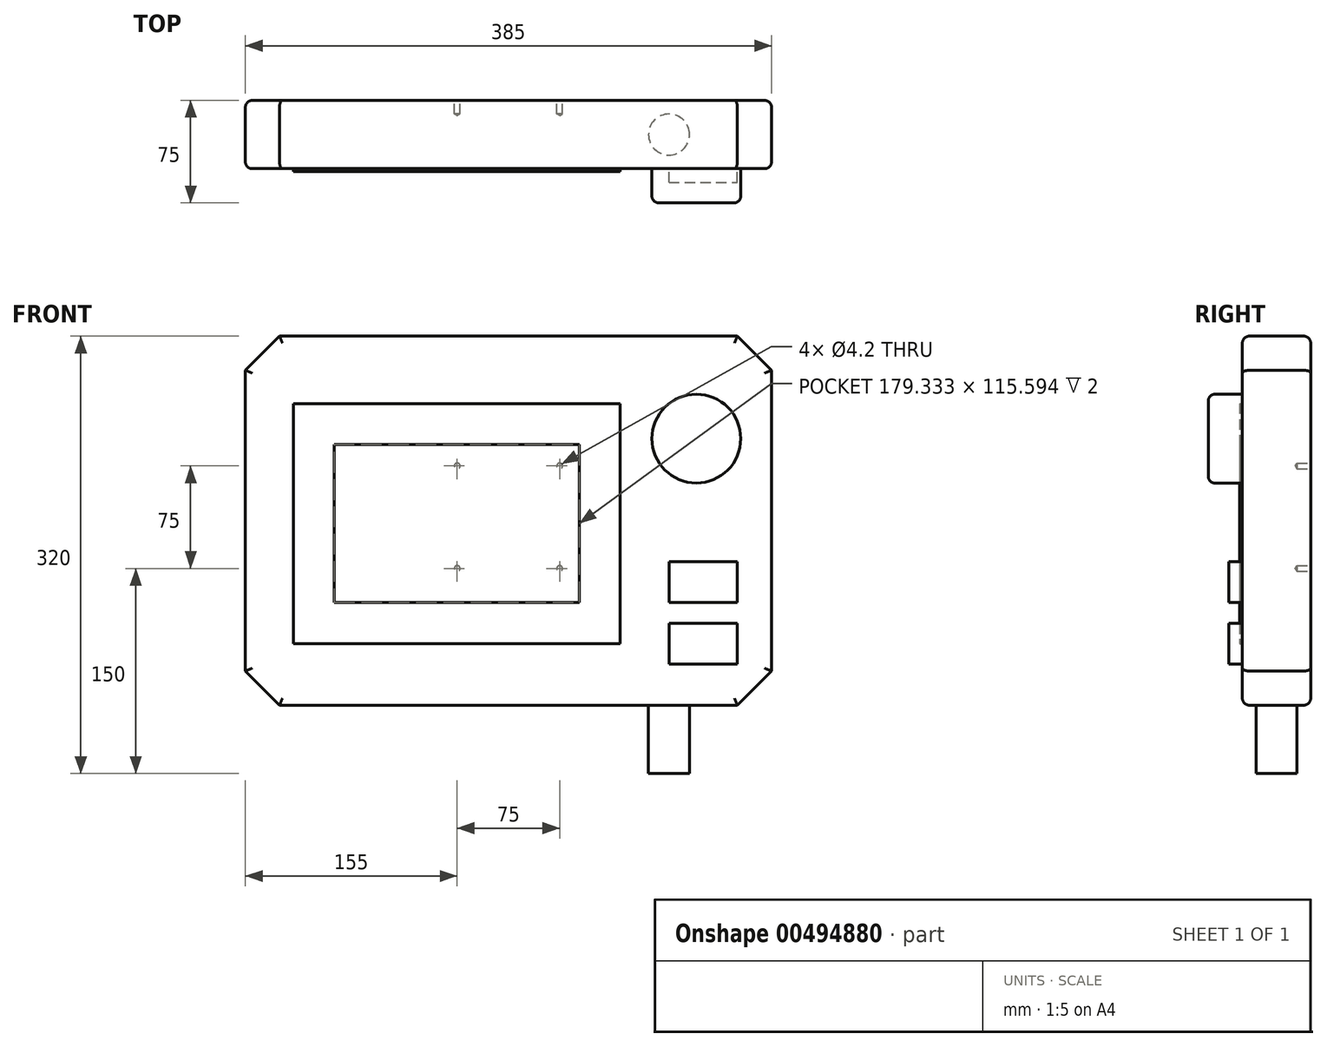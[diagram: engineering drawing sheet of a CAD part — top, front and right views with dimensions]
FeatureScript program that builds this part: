
annotation { "Feature Type Name" : "Feature", "Feature Type Description" : "" }
export const myFeature = defineFeature(function(context is Context, id is Id, definition is map)
    precondition{}
    {
        {
            var Q0;
            Q0=qCreatedBy(makeId("Front.planeOp"),FACE);
            var sketch = newSketch(context, id + "F0", { "sketchPlane" : qUnion([Q0])});
            skLineSegment(sketch, "E0.bottom", {"start": v(-192.5, 0) * mm, "end": v(192.5, 0) * mm});
            skLineSegment(sketch, "E0.top", {"start": v(-192.5, 270) * mm, "end": v(192.5, 270) * mm});
            skLineSegment(sketch, "E0.left", {"start": v(-192.5, 0) * mm, "end": v(-192.5, 270) * mm});
            skLineSegment(sketch, "E0.right", {"start": v(192.5, 0) * mm, "end": v(192.5, 270) * mm});
            skSolve(sketch);
        }
        {
            var Q0;
            Q0=qSketchRegion(id+"F0",true);
            extrude(context, id + "F1", {"entities" : qUnion([Q0]), "depth" : 50 * mm});
        }
        {
            var Q0;
            Q0=makeQuery(id+"F1.opExtrude","CAP_FACE",FACE,{"disambiguationData":[OSD([sQuery(id+"F0.wireOp",EDGE,"E0.bottom"),sQuery(id+"F0.wireOp",EDGE,"E0.top"),sQuery(id+"F0.wireOp",EDGE,"E0.left"),sQuery(id+"F0.wireOp",EDGE,"E0.right")])],"isStart":false});
            var sketch = newSketch(context, id + "F2", { "sketchPlane" : qUnion([Q0])});
            skLineSegment(sketch, "E1.bottom", {"start": v(-127.5, 190.6) * mm, "end": v(51.83, 190.6) * mm});
            skLineSegment(sketch, "E1.top", {"start": v(-127.5, 75) * mm, "end": v(51.83, 75) * mm});
            skLineSegment(sketch, "E1.left", {"start": v(-127.5, 190.6) * mm, "end": v(-127.5, 75) * mm});
            skLineSegment(sketch, "E1.right", {"start": v(51.83, 190.6) * mm, "end": v(51.83, 75) * mm});
            skLineSegment(sketch, "E2", {"start": v(-127.5, 75) * mm, "end": v(51.83, 190.6) * mm, "construction": true});
            skLineSegment(sketch, "E3.bottom", {"start": v(-157.5, 220.6) * mm, "end": v(81.83, 220.6) * mm});
            skLineSegment(sketch, "E3.top", {"start": v(-157.5, 45) * mm, "end": v(81.83, 45) * mm});
            skLineSegment(sketch, "E3.left", {"start": v(-157.5, 220.6) * mm, "end": v(-157.5, 45) * mm});
            skLineSegment(sketch, "E3.right", {"start": v(81.83, 220.6) * mm, "end": v(81.83, 45) * mm});
            skSolve(sketch);
        }
        {
            var Q0;
            Q0=qSketchRegion(id+"F2",true);
            extrude(context, id + "F3", {"entities" : qUnion([Q0]), "operationType" : NewBodyOperationType.ADD, "depth" : 2 * mm});
        }
        {
            var Q0;
            {var subQ0=sQuery(id+"F0.wireOp",EDGE,"E0.left");var subQ1=sQuery(id+"F0.wireOp",EDGE,"E0.top");var subQ2=sQuery(id+"F0.wireOp",EDGE,"E0.right");var subQ3=sQuery(id+"F0.wireOp",EDGE,"E0.bottom");Q0=makeQuery(id+"F3.boolean.opBoolean","SPLIT",FACE,{"disambiguationData":[TD([makeQuery(id+"F1.opExtrude","SWEPT_FACE",FACE,{"disambiguationData":[OSD([subQ3])]})])],"derivedFrom":makeQuery(id+"F1.opExtrude","CAP_FACE",FACE,{"disambiguationData":[OSD([subQ3,subQ1,subQ0,subQ2])],"isStart":false})});}
            var sketch = newSketch(context, id + "F4", { "sketchPlane" : qUnion([Q0])});
            skCircle(sketch, "E4", {"center": v(137.5, 195) * mm, "radius": 32.5 * mm});
            skSolve(sketch);
        }
        {
            var Q0;
            Q0=qSketchRegion(id+"F4",true);
            extrude(context, id + "F5", {"entities" : qUnion([Q0]), "operationType" : NewBodyOperationType.ADD, "depth" : 25 * mm});
        }
        {
            var Q0;
            {var subQ0=sQuery(id+"F0.wireOp",EDGE,"E0.left");var subQ1=sQuery(id+"F0.wireOp",EDGE,"E0.top");var subQ2=sQuery(id+"F0.wireOp",EDGE,"E0.right");var subQ3=sQuery(id+"F0.wireOp",EDGE,"E0.bottom");Q0=makeQuery(id+"F3.boolean.opBoolean","SPLIT",FACE,{"disambiguationData":[TD([makeQuery(id+"F1.opExtrude","SWEPT_FACE",FACE,{"disambiguationData":[OSD([subQ3])]})])],"derivedFrom":makeQuery(id+"F1.opExtrude","CAP_FACE",FACE,{"disambiguationData":[OSD([subQ3,subQ1,subQ0,subQ2])],"isStart":false})});}
            var sketch = newSketch(context, id + "F6", { "sketchPlane" : qUnion([Q0])});
            skLineSegment(sketch, "E5.bottom", {"start": v(117.5, 105) * mm, "end": v(167.5, 105) * mm});
            skLineSegment(sketch, "E5.top", {"start": v(117.5, 75) * mm, "end": v(167.5, 75) * mm});
            skLineSegment(sketch, "E5.left", {"start": v(117.5, 105) * mm, "end": v(117.5, 75) * mm});
            skLineSegment(sketch, "E5.right", {"start": v(167.5, 105) * mm, "end": v(167.5, 75) * mm});
            skLineSegment(sketch, "E6.bottom", {"start": v(117.5, 60) * mm, "end": v(167.5, 60) * mm});
            skLineSegment(sketch, "E6.top", {"start": v(117.5, 30) * mm, "end": v(167.5, 30) * mm});
            skLineSegment(sketch, "E6.left", {"start": v(117.5, 60) * mm, "end": v(117.5, 30) * mm});
            skLineSegment(sketch, "E6.right", {"start": v(167.5, 60) * mm, "end": v(167.5, 30) * mm});
            skSolve(sketch);
        }
        {
            var Q0;
            Q0=qSketchRegion(id+"F6",true);
            extrude(context, id + "F7", {"entities" : qUnion([Q0]), "operationType" : NewBodyOperationType.ADD, "depth" : 10 * mm});
        }
        {
            var Q0;
            Q0=makeQuery(id+"F1.opExtrude","SWEPT_EDGE",EDGE,{"disambiguationData":[OSD([sQuery(id+"F0.wireOp",EDGE,"E0.top"),sQuery(id+"F0.wireOp",EDGE,"E0.right")])]});
            var Q1;
            Q1=makeQuery(id+"F1.opExtrude","SWEPT_EDGE",EDGE,{"disambiguationData":[OSD([sQuery(id+"F0.wireOp",EDGE,"E0.top"),sQuery(id+"F0.wireOp",EDGE,"E0.left")])]});
            var Q2;
            Q2=makeQuery(id+"F1.opExtrude","SWEPT_EDGE",EDGE,{"disambiguationData":[OSD([sQuery(id+"F0.wireOp",EDGE,"E0.bottom"),sQuery(id+"F0.wireOp",EDGE,"E0.left")])]});
            var Q3;
            Q3=makeQuery(id+"F1.opExtrude","SWEPT_EDGE",EDGE,{"disambiguationData":[OSD([sQuery(id+"F0.wireOp",EDGE,"E0.bottom"),sQuery(id+"F0.wireOp",EDGE,"E0.right")])]});
            chamfer(context, id + "F8", {"entities" : qUnion([Q0, Q1, Q2, Q3]), "width" : 25 * mm, "tangentPropagation" : true});
        }
        {
            var Q0;
            Q0=makeQuery(id+"F5.opExtrude","CAP_EDGE",EDGE,{"disambiguationData":[OSD([sQuery(id+"F4.wireOp",EDGE,"E4")])],"isStart":false});
            fillet(context, id + "F9", {"entities" : qUnion([Q0]), "radius" : 5 * mm, "tangentPropagation" : true, "allowEdgeOverflow" : false});
        }
        {
            var Q0;
            Q0=makeQuery(id+"F1.opExtrude","SWEPT_FACE",FACE,{"disambiguationData":[OSD([sQuery(id+"F0.wireOp",EDGE,"E0.bottom")])]});
            var sketch = newSketch(context, id + "F10", { "sketchPlane" : qUnion([Q0])});
            skCircle(sketch, "E7", {"center": v(117.5, 25) * mm, "radius": 15 * mm});
            skSolve(sketch);
        }
        {
            var Q0;
            Q0=qSketchRegion(id+"F10",true);
            extrude(context, id + "F11", {"entities" : qUnion([Q0]), "operationType" : NewBodyOperationType.ADD, "depth" : 50 * mm});
        }
        {
            var Q0;
            Q0=makeQuery(id+"F1.opExtrude","CAP_FACE",FACE,{"disambiguationData":[OSD([sQuery(id+"F0.wireOp",EDGE,"E0.bottom"),sQuery(id+"F0.wireOp",EDGE,"E0.top"),sQuery(id+"F0.wireOp",EDGE,"E0.left"),sQuery(id+"F0.wireOp",EDGE,"E0.right")])],"isStart":true});
            var sketch = newSketch(context, id + "F12", { "sketchPlane" : qUnion([Q0])});
            skPoint(sketch, "E8", {"position": v(-37.5, 175) * mm});
            skPoint(sketch, "E9", {"position": v(-37.5, 100) * mm});
            skPoint(sketch, "E10", {"position": v(37.5, 100) * mm});
            skPoint(sketch, "E11", {"position": v(37.5, 175) * mm});
            skSolve(sketch);
        }
        {
            var Q0;
            Q0=sQuery(id+"F12.wireOp",VERTEX,"E8");
            var Q1;
            Q1=sQuery(id+"F12.wireOp",VERTEX,"E11");
            var Q2;
            Q2=sQuery(id+"F12.wireOp",VERTEX,"E10");
            var Q3;
            Q3=sQuery(id+"F12.wireOp",VERTEX,"E9");
            var Q4;
            Q4=makeQuery(id+"F1.opExtrude","SWEPT_BODY",BODY,{"disambiguationData":[OSD([sQuery(id+"F0.wireOp",EDGE,"E0.bottom"),sQuery(id+"F0.wireOp",EDGE,"E0.top"),sQuery(id+"F0.wireOp",EDGE,"E0.left"),sQuery(id+"F0.wireOp",EDGE,"E0.right")])]});
            hole(context, id + "F13", {"style" : HoleStyle.SIMPLE, "endStyle" : HoleEndStyle.BLIND, "standardTappedOrClearance" : lookupTablePath({ "standard" : "ISO", "size" : "4.2", "type" : "Drilled" }), "standardBlindInLast" : lookupTablePath({ "standard" : "ISO", "size" : "4.2", "type" : "Drilled" }), "holeDiameter" : 4.2 * mm, "holeDepth" : 10 * mm, "isTappedThrough" : true, "tappedDepth" : 7.6 * mm, "tapClearance" : 3, "locations" : qUnion([Q0, Q1, Q2, Q3]), "scope" : qUnion([Q4])});
        }
        {
            var Q0;
            Q0=makeQuery(id+"F1.opExtrude","CAP_EDGE",EDGE,{"disambiguationData":[OSD([sQuery(id+"F0.wireOp",EDGE,"E0.top")])],"isStart":true});
            var Q1;
            {var subQ0=sQuery(id+"F0.wireOp",EDGE,"E0.right");var subQ1=sQuery(id+"F0.wireOp",EDGE,"E0.top");Q1=makeQuery(id+"F8.opChamfer","BLEND_EDGE",EDGE,{"blendedFrom":[makeQuery(id+"F1.opExtrude","SWEPT_EDGE",EDGE,{"disambiguationData":[OSD([subQ1,subQ0])]}),makeQuery(id+"F1.opExtrude","CAP_FACE",FACE,{"disambiguationData":[OSD([sQuery(id+"F0.wireOp",EDGE,"E0.bottom"),subQ1,sQuery(id+"F0.wireOp",EDGE,"E0.left"),subQ0])],"isStart":true})],"blendedInto":[makeQuery(id+"F1.opExtrude","CAP_FACE",FACE,{"disambiguationData":[OSD([sQuery(id+"F0.wireOp",EDGE,"E0.bottom"),subQ1,sQuery(id+"F0.wireOp",EDGE,"E0.left"),subQ0])],"isStart":true})]});}
            var Q2;
            Q2=makeQuery(id+"F1.opExtrude","CAP_EDGE",EDGE,{"disambiguationData":[OSD([sQuery(id+"F0.wireOp",EDGE,"E0.right")])],"isStart":true});
            var Q3;
            {var subQ0=sQuery(id+"F0.wireOp",EDGE,"E0.right");var subQ1=sQuery(id+"F0.wireOp",EDGE,"E0.bottom");Q3=makeQuery(id+"F8.opChamfer","BLEND_EDGE",EDGE,{"blendedFrom":[makeQuery(id+"F1.opExtrude","SWEPT_EDGE",EDGE,{"disambiguationData":[OSD([subQ1,subQ0])]}),makeQuery(id+"F1.opExtrude","CAP_FACE",FACE,{"disambiguationData":[OSD([subQ1,sQuery(id+"F0.wireOp",EDGE,"E0.top"),sQuery(id+"F0.wireOp",EDGE,"E0.left"),subQ0])],"isStart":true})],"blendedInto":[makeQuery(id+"F1.opExtrude","CAP_FACE",FACE,{"disambiguationData":[OSD([subQ1,sQuery(id+"F0.wireOp",EDGE,"E0.top"),sQuery(id+"F0.wireOp",EDGE,"E0.left"),subQ0])],"isStart":true})]});}
            var Q4;
            Q4=makeQuery(id+"F1.opExtrude","CAP_EDGE",EDGE,{"disambiguationData":[OSD([sQuery(id+"F0.wireOp",EDGE,"E0.bottom")])],"isStart":true});
            var Q5;
            {var subQ0=sQuery(id+"F0.wireOp",EDGE,"E0.left");var subQ1=sQuery(id+"F0.wireOp",EDGE,"E0.top");Q5=makeQuery(id+"F8.opChamfer","BLEND_EDGE",EDGE,{"blendedFrom":[makeQuery(id+"F1.opExtrude","SWEPT_EDGE",EDGE,{"disambiguationData":[OSD([subQ1,subQ0])]}),makeQuery(id+"F1.opExtrude","CAP_FACE",FACE,{"disambiguationData":[OSD([sQuery(id+"F0.wireOp",EDGE,"E0.bottom"),subQ1,subQ0,sQuery(id+"F0.wireOp",EDGE,"E0.right")])],"isStart":true})],"blendedInto":[makeQuery(id+"F1.opExtrude","CAP_FACE",FACE,{"disambiguationData":[OSD([sQuery(id+"F0.wireOp",EDGE,"E0.bottom"),subQ1,subQ0,sQuery(id+"F0.wireOp",EDGE,"E0.right")])],"isStart":true})]});}
            var Q6;
            Q6=makeQuery(id+"F1.opExtrude","CAP_EDGE",EDGE,{"disambiguationData":[OSD([sQuery(id+"F0.wireOp",EDGE,"E0.left")])],"isStart":true});
            var Q7;
            {var subQ0=sQuery(id+"F0.wireOp",EDGE,"E0.left");var subQ1=sQuery(id+"F0.wireOp",EDGE,"E0.bottom");Q7=makeQuery(id+"F8.opChamfer","BLEND_EDGE",EDGE,{"blendedFrom":[makeQuery(id+"F1.opExtrude","SWEPT_EDGE",EDGE,{"disambiguationData":[OSD([subQ1,subQ0])]}),makeQuery(id+"F1.opExtrude","CAP_FACE",FACE,{"disambiguationData":[OSD([subQ1,sQuery(id+"F0.wireOp",EDGE,"E0.top"),subQ0,sQuery(id+"F0.wireOp",EDGE,"E0.right")])],"isStart":true})],"blendedInto":[makeQuery(id+"F1.opExtrude","CAP_FACE",FACE,{"disambiguationData":[OSD([subQ1,sQuery(id+"F0.wireOp",EDGE,"E0.top"),subQ0,sQuery(id+"F0.wireOp",EDGE,"E0.right")])],"isStart":true})]});}
            var Q8;
            {var subQ0=sQuery(id+"F0.wireOp",EDGE,"E0.left");var subQ1=sQuery(id+"F0.wireOp",EDGE,"E0.top");var subQ2=sQuery(id+"F0.wireOp",EDGE,"E0.right");var subQ3=sQuery(id+"F0.wireOp",EDGE,"E0.bottom");Q8=makeQuery(id+"F8.opChamfer","BLEND_EDGE",EDGE,{"blendedFrom":[makeQuery(id+"F1.opExtrude","SWEPT_EDGE",EDGE,{"disambiguationData":[OSD([subQ1,subQ2])]}),makeQuery(id+"F3.boolean.opBoolean","SPLIT",FACE,{"disambiguationData":[TD([makeQuery(id+"F1.opExtrude","SWEPT_FACE",FACE,{"disambiguationData":[OSD([subQ3])]})])],"derivedFrom":makeQuery(id+"F1.opExtrude","CAP_FACE",FACE,{"disambiguationData":[OSD([subQ3,subQ1,subQ0,subQ2])],"isStart":false})})],"blendedInto":[makeQuery(id+"F3.boolean.opBoolean","SPLIT",FACE,{"disambiguationData":[TD([makeQuery(id+"F1.opExtrude","SWEPT_FACE",FACE,{"disambiguationData":[OSD([subQ3])]})])],"derivedFrom":makeQuery(id+"F1.opExtrude","CAP_FACE",FACE,{"disambiguationData":[OSD([subQ3,subQ1,subQ0,subQ2])],"isStart":false})})]});}
            var Q9;
            Q9=makeQuery(id+"F1.opExtrude","CAP_EDGE",EDGE,{"disambiguationData":[OSD([sQuery(id+"F0.wireOp",EDGE,"E0.right")])],"isStart":false});
            var Q10;
            {var subQ0=sQuery(id+"F0.wireOp",EDGE,"E0.left");var subQ1=sQuery(id+"F0.wireOp",EDGE,"E0.top");var subQ2=sQuery(id+"F0.wireOp",EDGE,"E0.right");var subQ3=sQuery(id+"F0.wireOp",EDGE,"E0.bottom");Q10=makeQuery(id+"F8.opChamfer","BLEND_EDGE",EDGE,{"blendedFrom":[makeQuery(id+"F1.opExtrude","SWEPT_EDGE",EDGE,{"disambiguationData":[OSD([subQ3,subQ2])]}),makeQuery(id+"F3.boolean.opBoolean","SPLIT",FACE,{"disambiguationData":[TD([makeQuery(id+"F1.opExtrude","SWEPT_FACE",FACE,{"disambiguationData":[OSD([subQ3])]})])],"derivedFrom":makeQuery(id+"F1.opExtrude","CAP_FACE",FACE,{"disambiguationData":[OSD([subQ3,subQ1,subQ0,subQ2])],"isStart":false})})],"blendedInto":[makeQuery(id+"F3.boolean.opBoolean","SPLIT",FACE,{"disambiguationData":[TD([makeQuery(id+"F1.opExtrude","SWEPT_FACE",FACE,{"disambiguationData":[OSD([subQ3])]})])],"derivedFrom":makeQuery(id+"F1.opExtrude","CAP_FACE",FACE,{"disambiguationData":[OSD([subQ3,subQ1,subQ0,subQ2])],"isStart":false})})]});}
            var Q11;
            Q11=makeQuery(id+"F1.opExtrude","CAP_EDGE",EDGE,{"disambiguationData":[OSD([sQuery(id+"F0.wireOp",EDGE,"E0.bottom")])],"isStart":false});
            var Q12;
            {var subQ0=sQuery(id+"F0.wireOp",EDGE,"E0.left");var subQ1=sQuery(id+"F0.wireOp",EDGE,"E0.top");var subQ2=sQuery(id+"F0.wireOp",EDGE,"E0.right");var subQ3=sQuery(id+"F0.wireOp",EDGE,"E0.bottom");Q12=makeQuery(id+"F8.opChamfer","BLEND_EDGE",EDGE,{"blendedFrom":[makeQuery(id+"F1.opExtrude","SWEPT_EDGE",EDGE,{"disambiguationData":[OSD([subQ3,subQ0])]}),makeQuery(id+"F3.boolean.opBoolean","SPLIT",FACE,{"disambiguationData":[TD([makeQuery(id+"F1.opExtrude","SWEPT_FACE",FACE,{"disambiguationData":[OSD([subQ3])]})])],"derivedFrom":makeQuery(id+"F1.opExtrude","CAP_FACE",FACE,{"disambiguationData":[OSD([subQ3,subQ1,subQ0,subQ2])],"isStart":false})})],"blendedInto":[makeQuery(id+"F3.boolean.opBoolean","SPLIT",FACE,{"disambiguationData":[TD([makeQuery(id+"F1.opExtrude","SWEPT_FACE",FACE,{"disambiguationData":[OSD([subQ3])]})])],"derivedFrom":makeQuery(id+"F1.opExtrude","CAP_FACE",FACE,{"disambiguationData":[OSD([subQ3,subQ1,subQ0,subQ2])],"isStart":false})})]});}
            var Q13;
            Q13=makeQuery(id+"F1.opExtrude","CAP_EDGE",EDGE,{"disambiguationData":[OSD([sQuery(id+"F0.wireOp",EDGE,"E0.left")])],"isStart":false});
            var Q14;
            {var subQ0=sQuery(id+"F0.wireOp",EDGE,"E0.left");var subQ1=sQuery(id+"F0.wireOp",EDGE,"E0.top");var subQ2=sQuery(id+"F0.wireOp",EDGE,"E0.right");var subQ3=sQuery(id+"F0.wireOp",EDGE,"E0.bottom");Q14=makeQuery(id+"F8.opChamfer","BLEND_EDGE",EDGE,{"blendedFrom":[makeQuery(id+"F1.opExtrude","SWEPT_EDGE",EDGE,{"disambiguationData":[OSD([subQ1,subQ0])]}),makeQuery(id+"F3.boolean.opBoolean","SPLIT",FACE,{"disambiguationData":[TD([makeQuery(id+"F1.opExtrude","SWEPT_FACE",FACE,{"disambiguationData":[OSD([subQ3])]})])],"derivedFrom":makeQuery(id+"F1.opExtrude","CAP_FACE",FACE,{"disambiguationData":[OSD([subQ3,subQ1,subQ0,subQ2])],"isStart":false})})],"blendedInto":[makeQuery(id+"F3.boolean.opBoolean","SPLIT",FACE,{"disambiguationData":[TD([makeQuery(id+"F1.opExtrude","SWEPT_FACE",FACE,{"disambiguationData":[OSD([subQ3])]})])],"derivedFrom":makeQuery(id+"F1.opExtrude","CAP_FACE",FACE,{"disambiguationData":[OSD([subQ3,subQ1,subQ0,subQ2])],"isStart":false})})]});}
            var Q15;
            Q15=makeQuery(id+"F1.opExtrude","CAP_EDGE",EDGE,{"disambiguationData":[OSD([sQuery(id+"F0.wireOp",EDGE,"E0.top")])],"isStart":false});
            fillet(context, id + "F14", {"entities" : qUnion([Q0, Q1, Q2, Q3, Q4, Q5, Q6, Q7, Q8, Q9, Q10, Q11, Q12, Q13, Q14, Q15]), "radius" : 5 * mm, "tangentPropagation" : true, "allowEdgeOverflow" : false});
        }
    });
